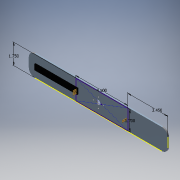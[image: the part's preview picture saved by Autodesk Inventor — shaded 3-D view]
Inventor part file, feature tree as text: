
AUTODESK INVENTOR PART (.ipt)
format: ipt  version: 2016 (Build 200138000, 138)  size: 228,352 bytes
history: native  units: in
note: dims shown in document units (in); Inventor stores cm internally (conversion verified against a paired STEP export)
features: sketch x7, extrude x6, fillet x1
ambient origin geometry x8: Origin, YZ Plane, XZ Plane, XY Plane, X Axis, Y Axis, Z Axis, Center Point
bodies: Solid1 (feature_tree)
feature tree (14):
  extrude  "Extrusion1"  Depth=1.8in
  extrude  "Extrusion2"  Depth=0.11in
  extrude  "Extrusion3"  Depth=3.7in
  extrude  "Extrusion4"  Depth=0.3937in
  extrude  "Extrusion5"  Depth=0.1in TaperAngle=0.0deg
  fillet  "Fillet1"  Radius=0.75in
  extrude  "Extrusion6"  Depth=0.5in
  sketch  "Sketch9"  dims[d37=0.133in d38=0.133in d39=0.133in d40=0.133in d45=0.35in d46=0.0in d47=0.37in d48=0.39in d49=0.95in d50=0.127in d51=0.0in d56=0.65in d57=0.5794in d58=0.0811in d59=0.0742in d60=0.0434in d63=0.0811in d64=0.0742in d65=4.2361in d66=4.1618in d67=4.2361in d68=0.6472in d69=4.5in d70=1.7in d73=0.5in d76=1.75in d77=3.45in d78=0.5in d79=0.5in d81=0.5in d82=0.5in d83=0.0in]
  sketch  "Sketch1"  dims[d0=12.0in d1=1.8in]
  sketch  "Sketch2"  dims[d2=0.11in d3=0.0in d4=3.0in]
  sketch  "Sketch5"  dims[d7=0.474in d8=1.5748in d10=0.105in d11=0.3937in d13=1.0in]
  sketch  "Sketch6"  dims[d15=0.4in d16=0.0in]
  sketch  "Sketch8"  dims[d17=3.0in d18=1.4in d19=3.7in d20=0.474in d21=0.105in d22=1.0in d25=0.1in d26=0.0in d35=0.75in d36=0.0in]
  sketch  "Sketch3"  dims[d5=1.4in d6=3.7in]
